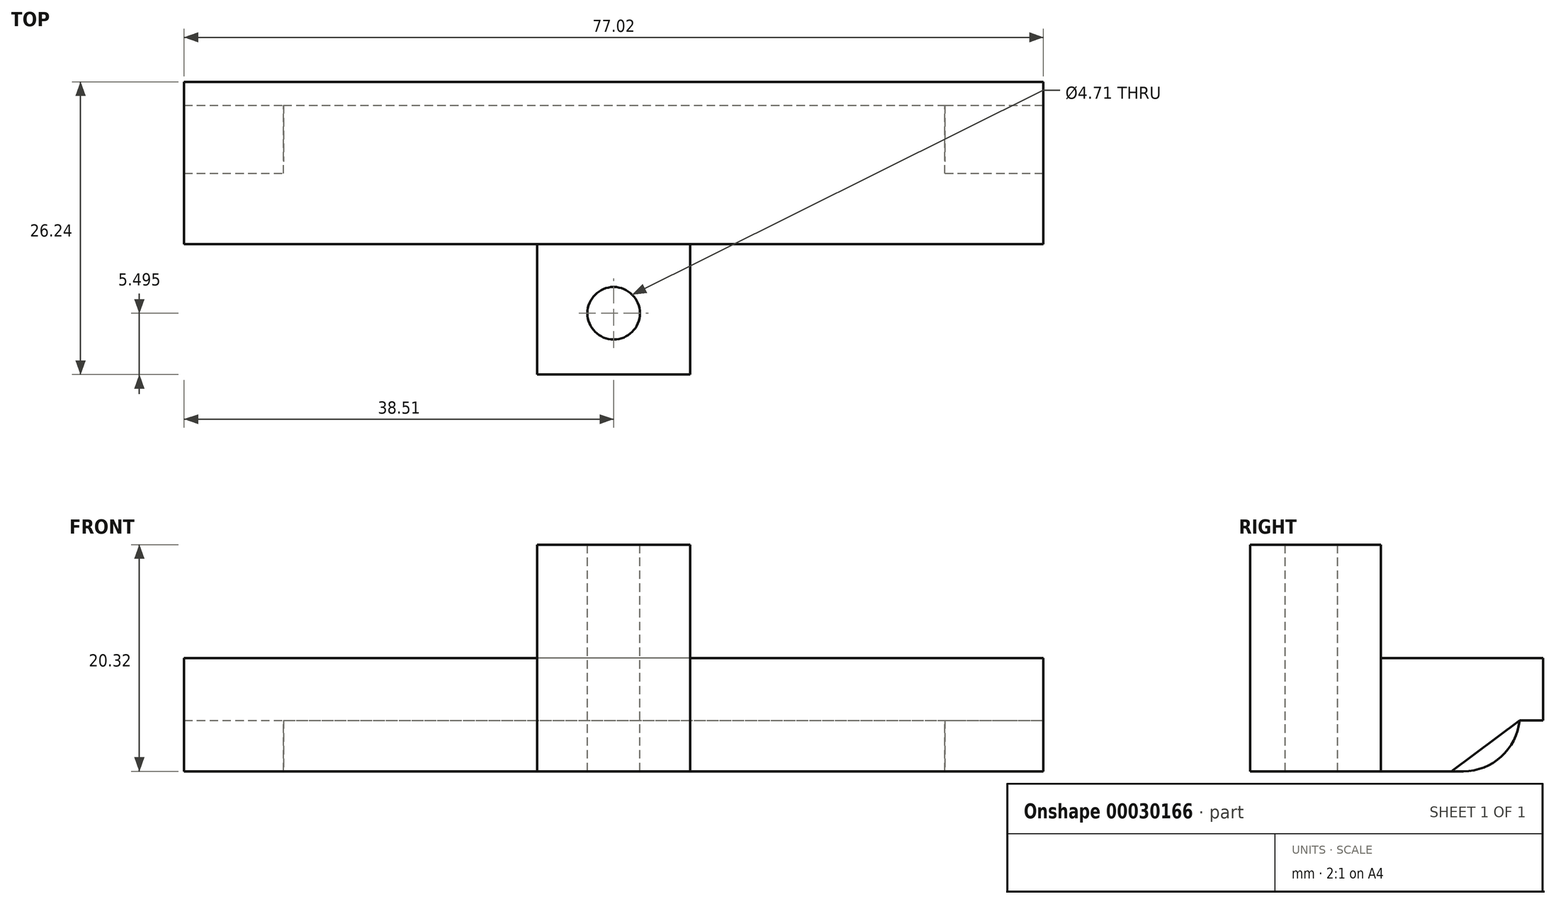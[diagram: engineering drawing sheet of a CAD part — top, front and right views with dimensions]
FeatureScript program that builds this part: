
annotation { "Feature Type Name" : "Feature", "Feature Type Description" : "" }
export const myFeature = defineFeature(function(context is Context, id is Id, definition is map)
    precondition{}
    {
        {
            var Q0;
            Q0=qCreatedBy(makeId("Top.planeOp"),FACE);
            var sketch = newSketch(context, id + "F0", { "sketchPlane" : qUnion([Q0])});
            skLineSegment(sketch, "E0.rect.bottom", {"start": v(38.5, 7.27) * mm, "end": v(-38.5, 7.27) * mm});
            skLineSegment(sketch, "E0.rect.top", {"start": v(38.5, -7.27) * mm, "end": v(-38.5, -7.27) * mm});
            skLineSegment(sketch, "E0.rect.left", {"start": v(38.5, 7.27) * mm, "end": v(38.5, -7.27) * mm});
            skLineSegment(sketch, "E0.rect.right", {"start": v(-38.5, 7.27) * mm, "end": v(-38.5, -7.27) * mm});
            skPoint(sketch, "E0.rect.middle", {"position": v(0, 0) * mm});
            skLineSegment(sketch, "E1.rect.bottom", {"start": v(6.85, -18.97) * mm, "end": v(-6.85, -18.97) * mm});
            skLineSegment(sketch, "E1.rect.left", {"start": v(6.85, -18.97) * mm, "end": v(6.85, -7.27) * mm});
            skLineSegment(sketch, "E1.rect.right", {"start": v(-6.85, -18.97) * mm, "end": v(-6.85, -7.27) * mm});
            skPoint(sketch, "E1.rect.middle", {"position": v(0, -7.27) * mm});
            skPoint(sketch, "E1.rect.top.end.orphan", {"position": v(-6.85, 4.42) * mm});
            skPoint(sketch, "E1.rect.top.start.orphan", {"position": v(6.85, 4.42) * mm});
            skSolve(sketch);
        }
        {
            var Q0;
            Q0=makeQuery(id+"F0.imprint","IMPRINT",FACE,{"disambiguationData":[TD([[makeQuery(id+"F0.imprint","IMPRINT",EDGE,{"derivedFrom":sQuery(id+"F0.wireOp",EDGE,"E0.rect.bottom")}),1.0]])]});
            extrude(context, id + "F1", {"entities" : qUnion([Q0]), "depth" : 10.16 * mm});
        }
        {
            var Q0;
            Q0=makeQuery(id+"F0.imprint","IMPRINT",FACE,{"disambiguationData":[TD([[makeQuery(id+"F0.imprint","IMPRINT",EDGE,{"derivedFrom":sQuery(id+"F0.wireOp",EDGE,"E1.rect.bottom")}),-1.0]])]});
            extrude(context, id + "F2", {"entities" : qUnion([Q0]), "operationType" : NewBodyOperationType.ADD, "depth" : 20.32 * mm});
        }
        {
            var Q0;
            Q0=makeQuery(id+"F1.opExtrude","SWEPT_FACE",FACE,{"disambiguationData":[OSD([sQuery(id+"F0.wireOp",EDGE,"E0.rect.left")])]});
            var sketch = newSketch(context, id + "F3", { "sketchPlane" : qUnion([Q0])});
            skLineSegment(sketch, "E2", {"start": v(1.65, 1.93) * mm, "end": v(5.18, 4.57) * mm});
            skLineSegment(sketch, "E3", {"start": v(5.18, 4.57) * mm, "end": v(7.27, 4.57) * mm});
            skLineSegment(sketch, "E4", {"start": v(5.18, 4.57) * mm, "end": v(-0.93, 0) * mm});
            skSolve(sketch);
        }
        {
            var Q0;
            {var subQ6=sQuery(id+"F3.wireOp",EDGE,"E3");Q0=makeQuery(id+"F3.imprint","IMPRINT",FACE,{"disambiguationData":[TD([[makeQuery(id+"F3.imprint","IMPRINT",EDGE,{"derivedFrom":subQ6}),-1.0]])]});}
            extrude(context, id + "F4", {"entities" : qUnion([Q0]), "operationType" : NewBodyOperationType.REMOVE, "endBound" : BoundingType.THROUGH_ALL, "oppositeDirection" : true, "depth" : 25.4 * mm});
        }
        {
            var Q0;
            Q0=makeQuery(id+"F4.boolean.opBoolean","COPY",FACE,{"derivedFrom":makeQuery(id+"F4.opExtrude","SWEPT_FACE",FACE,{"disambiguationData":[OSD([sQuery(id+"F3.wireOp",EDGE,"E3")])]})});
            var sketch = newSketch(context, id + "F5", { "sketchPlane" : qUnion([Q0])});
            skLineSegment(sketch, "E5.bottom", {"start": v(-29.6, -5.18) * mm, "end": v(29.7, -5.18) * mm});
            skLineSegment(sketch, "E5.top", {"start": v(-29.6, 2.88) * mm, "end": v(29.7, 2.88) * mm});
            skLineSegment(sketch, "E5.left", {"start": v(-29.6, -5.18) * mm, "end": v(-29.6, 2.88) * mm});
            skLineSegment(sketch, "E5.right", {"start": v(29.7, -5.18) * mm, "end": v(29.7, 2.88) * mm});
            skSolve(sketch);
        }
        {
            var Q0;
            Q0 = qSketchRegion(id + "F5", true);
            var Q1;
            {var subQ0=sQuery(id+"F0.wireOp",EDGE,"E0.rect.top");Q1=makeQuery(id+"F2.boolean.opBoolean","MERGE",FACE,{"derivedFrom":[makeQuery(id+"F1.opExtrude","CAP_FACE",FACE,{"disambiguationData":[OSD([sQuery(id+"F0.wireOp",EDGE,"E0.rect.bottom"),subQ0,sQuery(id+"F0.wireOp",EDGE,"E0.rect.left"),sQuery(id+"F0.wireOp",EDGE,"E0.rect.right")])],"isStart":true}),makeQuery(id+"F2.opExtrude","CAP_FACE",FACE,{"disambiguationData":[OSD([subQ0,sQuery(id+"F0.wireOp",EDGE,"E1.rect.bottom"),sQuery(id+"F0.wireOp",EDGE,"E1.rect.left"),sQuery(id+"F0.wireOp",EDGE,"E1.rect.right")])],"isStart":true})]});}
            var Q2;
            Q2=makeQuery(id+"F1.opExtrude","SWEPT_BODY",BODY,{"disambiguationData":[OSD([sQuery(id+"F0.wireOp",EDGE,"E0.rect.bottom"),sQuery(id+"F0.wireOp",EDGE,"E0.rect.top"),sQuery(id+"F0.wireOp",EDGE,"E0.rect.left"),sQuery(id+"F0.wireOp",EDGE,"E0.rect.right")])]});
            extrude(context, id + "F6", {"entities" : qUnion([Q0]), "operationType" : NewBodyOperationType.ADD, "endBound" : BoundingType.UP_TO_SURFACE, "endBoundEntityFace" : qUnion([Q1]), "endBoundEntityBody" : qUnion([Q2]), "depth" : 6.35 * mm});
        }
        {
            var Q0;
            Q0=makeQuery(id+"F6.opExtrude","CAP_EDGE",EDGE,{"disambiguationData":[OSD([sQuery(id+"F5.wireOp",EDGE,"E5.bottom")])],"isStart":false});
            fillet(context, id + "F7", {"entities" : qUnion([Q0]), "radius" : 5.08 * mm, "tangentPropagation" : true, "allowEdgeOverflow" : false});
        }
        {
            var Q0;
            Q0=makeQuery(id+"F2.opExtrude","CAP_FACE",FACE,{"disambiguationData":[OSD([sQuery(id+"F0.wireOp",EDGE,"E0.rect.top"),sQuery(id+"F0.wireOp",EDGE,"E1.rect.bottom"),sQuery(id+"F0.wireOp",EDGE,"E1.rect.left"),sQuery(id+"F0.wireOp",EDGE,"E1.rect.right")])],"isStart":false});
            var sketch = newSketch(context, id + "F8", { "sketchPlane" : qUnion([Q0])});
            skCircle(sketch, "E6", {"center": v(0, -13.48) * mm, "radius": 2.35 * mm});
            skSolve(sketch);
        }
        {
            var Q0;
            Q0 = qSketchRegion(id + "F8", true);
            extrude(context, id + "F9", {"entities" : qUnion([Q0]), "operationType" : NewBodyOperationType.REMOVE, "endBound" : BoundingType.THROUGH_ALL, "oppositeDirection" : true, "depth" : 25.4 * mm});
        }
    });
